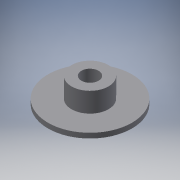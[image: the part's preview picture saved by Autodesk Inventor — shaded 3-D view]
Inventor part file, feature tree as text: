
AUTODESK INVENTOR PART (.ipt)
format: ipt  version: 2016 (Build 200138000, 138)  size: 102,912 bytes
history: native  units: mm
features: extrude x3, sketch x3
ambient origin geometry x8: Origin, YZ Plane, XZ Plane, XY Plane, X Axis, Y Axis, Z Axis, Center Point
bodies: Solid1 (feature_tree)
feature tree (6):
  extrude  "Extrusion1"  Depth=5.0mm TaperAngle=0.0deg
  extrude  "Extrusion2"  Depth=4.0mm TaperAngle=0.0deg
  extrude  "Extrusion3"  Depth=5.0mm TaperAngle=0.0deg
  sketch  "Sketch1"  dims[d0=17.0mm d1=5.0mm d2=0.0mm]
  sketch  "Sketch2"  dims[d3=7.5mm d4=4.0mm d5=0.0mm]
  sketch  "Sketch3"  dims[d6=3.5mm d7=5.0mm d8=0.0mm]
